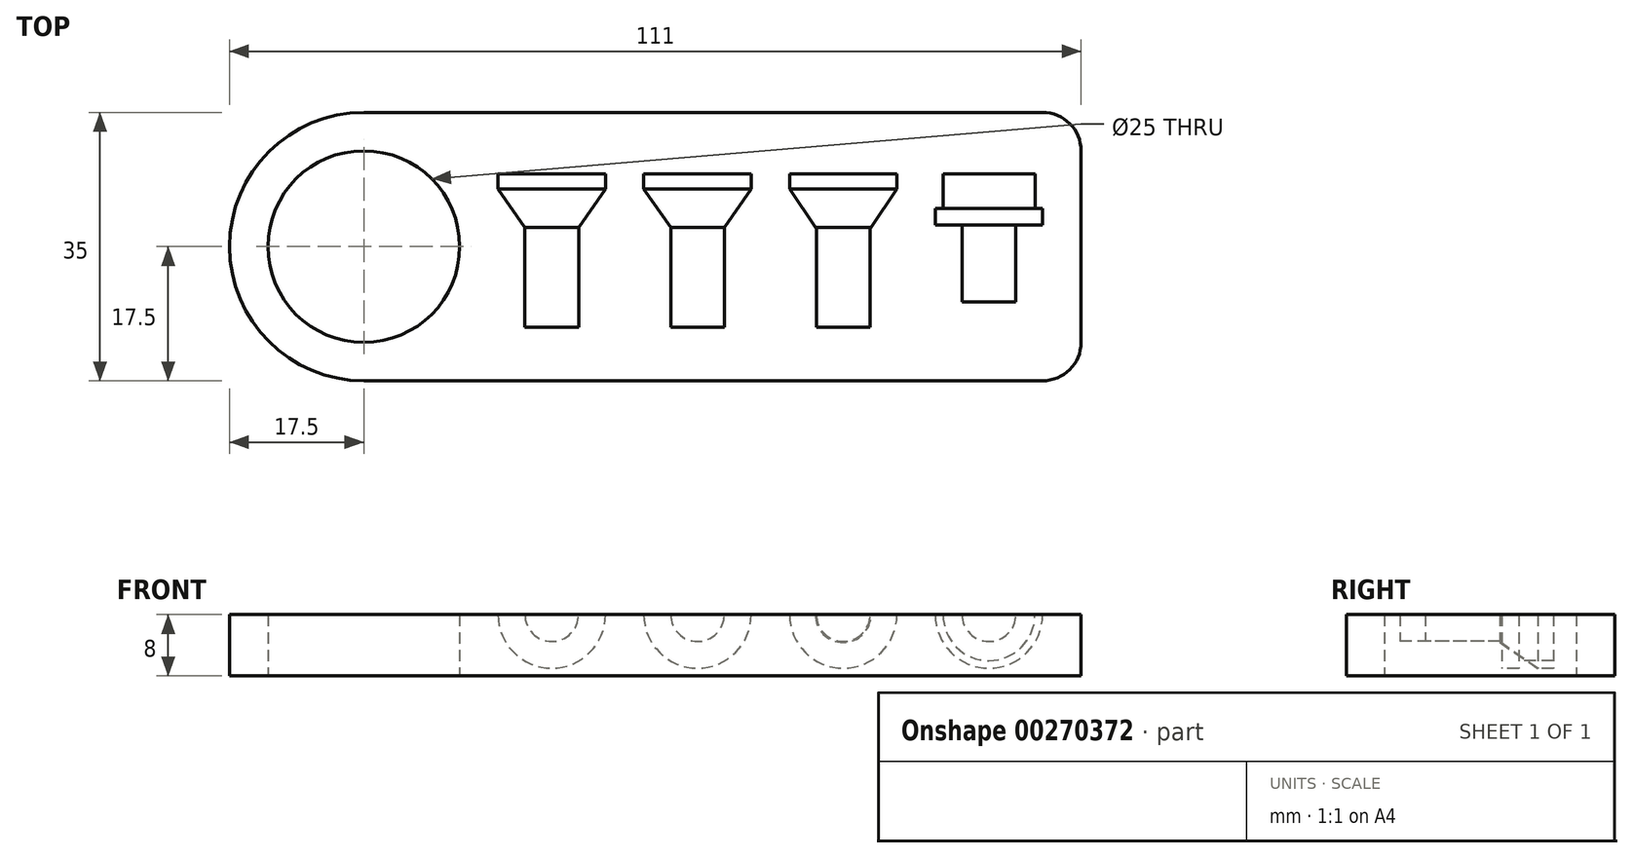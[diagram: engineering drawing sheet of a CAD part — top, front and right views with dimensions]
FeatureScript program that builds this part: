
annotation { "Feature Type Name" : "Feature", "Feature Type Description" : "" }
export const myFeature = defineFeature(function(context is Context, id is Id, definition is map)
    precondition{}
    {
        {
            var Q0;
            Q0=qCreatedBy(makeId("Top.planeOp"),FACE);
            var sketch = newSketch(context, id + "F0", { "sketchPlane" : qUnion([Q0])});
            skLineSegment(sketch, "E0.bottom", {"start": v(17.5, 0) * mm, "end": v(106, 0) * mm});
            skLineSegment(sketch, "E0.top", {"start": v(17.5, 35) * mm, "end": v(106, 35) * mm});
            skLineSegment(sketch, "E0.left", {"start": v(0, 17.5) * mm, "end": v(0, 17.5) * mm});
            skLineSegment(sketch, "E0.right", {"start": v(111, 5) * mm, "end": v(111, 30) * mm});
            skLineSegment(sketch, "E1.bottom", {"start": v(0, 0) * mm, "end": v(17.5, 0) * mm, "construction": true});
            skLineSegment(sketch, "E1.top", {"start": v(0, 17.5) * mm, "end": v(17.5, 17.5) * mm, "construction": true});
            skLineSegment(sketch, "E1.left", {"start": v(0, 0) * mm, "end": v(0, 17.5) * mm, "construction": true});
            skLineSegment(sketch, "E1.right", {"start": v(17.5, 0) * mm, "end": v(17.5, 17.5) * mm, "construction": true});
            skCircle(sketch, "E2", {"center": v(17.5, 17.5) * mm, "radius": 12.5 * mm});
            skPoint(sketch, "E3.visualSharp", {"position": v(0, 0) * mm});
            skArc(sketch, "E3.filletArc", {"start": v(0, 17.5) * mm, "mid": v(5.13, 5.13) * mm, "end": v(17.5, 0) * mm});
            skPoint(sketch, "E4.visualSharp", {"position": v(0, 35) * mm});
            skArc(sketch, "E4.filletArc", {"start": v(17.5, 35) * mm, "mid": v(5.13, 29.87) * mm, "end": v(0, 17.5) * mm});
            skPoint(sketch, "E5.visualSharp", {"position": v(111, 35) * mm});
            skArc(sketch, "E5.filletArc", {"start": v(111, 30) * mm, "mid": v(109.54, 33.54) * mm, "end": v(106, 35) * mm});
            skPoint(sketch, "E6.visualSharp", {"position": v(111, 0) * mm});
            skArc(sketch, "E6.filletArc", {"start": v(106, 0) * mm, "mid": v(109.54, 1.46) * mm, "end": v(111, 5) * mm});
            skSolve(sketch);
        }
        {
            var Q0;
            Q0=makeQuery(id+"F0.imprint","IMPRINT",FACE,{"disambiguationData":[TD([[makeQuery(id+"F0.imprint","IMPRINT",EDGE,{"derivedFrom":sQuery(id+"F0.wireOp",EDGE,"E0.bottom")}),1.0]])]});
            extrude(context, id + "F1", {"entities" : qUnion([Q0]), "depth" : 8 * mm});
        }
        {
            var Q0;
            Q0=makeQuery(id+"F1.opExtrude","CAP_FACE",FACE,{"disambiguationData":[OSD([sQuery(id+"F0.wireOp",EDGE,"E0.bottom"),sQuery(id+"F0.wireOp",EDGE,"E0.top"),sQuery(id+"F0.wireOp",EDGE,"E0.right"),sQuery(id+"F0.wireOp",EDGE,"E2"),sQuery(id+"F0.wireOp",EDGE,"E3.filletArc"),sQuery(id+"F0.wireOp",EDGE,"E4.filletArc"),sQuery(id+"F0.wireOp",EDGE,"E5.filletArc"),sQuery(id+"F0.wireOp",EDGE,"E6.filletArc")])],"isStart":false});
            var sketch = newSketch(context, id + "F2", { "sketchPlane" : qUnion([Q0])});
            skLineSegment(sketch, "E7.bottom", {"start": v(0, 0) * mm, "end": v(42, 0) * mm, "construction": true});
            skLineSegment(sketch, "E7.top", {"start": v(0, 27) * mm, "end": v(42, 27) * mm, "construction": true});
            skLineSegment(sketch, "E7.left", {"start": v(0, 0) * mm, "end": v(0, 27) * mm, "construction": true});
            skLineSegment(sketch, "E7.right", {"start": v(42, 0) * mm, "end": v(42, 27) * mm, "construction": true});
            skLineSegment(sketch, "E8.bottom", {"start": v(42, 27) * mm, "end": v(49, 27) * mm});
            skLineSegment(sketch, "E8.left", {"start": v(42, 27) * mm, "end": v(42, 25) * mm});
            skLineSegment(sketch, "E8.right", {"start": v(49, 27) * mm, "end": v(49, 25) * mm});
            skLineSegment(sketch, "E9", {"start": v(42, 27) * mm, "end": v(61, 27) * mm, "construction": true});
            skLineSegment(sketch, "E10", {"start": v(61, 27) * mm, "end": v(80, 27) * mm, "construction": true});
            skLineSegment(sketch, "E11.bottom", {"start": v(61, 27) * mm, "end": v(68, 27) * mm});
            skLineSegment(sketch, "E11.left", {"start": v(61, 27) * mm, "end": v(61, 25) * mm});
            skLineSegment(sketch, "E11.right", {"start": v(68, 27) * mm, "end": v(68, 25) * mm});
            skLineSegment(sketch, "E12.bottom", {"start": v(80, 27) * mm, "end": v(87, 27) * mm});
            skLineSegment(sketch, "E12.left", {"start": v(80, 27) * mm, "end": v(80, 25) * mm});
            skLineSegment(sketch, "E12.right", {"start": v(87, 27) * mm, "end": v(87, 25) * mm});
            skLineSegment(sketch, "E13.left", {"start": v(42, 25) * mm, "end": v(42, 20) * mm});
            skLineSegment(sketch, "E14.left", {"start": v(61, 25) * mm, "end": v(61, 20) * mm});
            skLineSegment(sketch, "E15.top", {"start": v(83.5, 20) * mm, "end": v(83.63, 20) * mm});
            skLineSegment(sketch, "E15.left", {"start": v(80, 25) * mm, "end": v(80, 20) * mm});
            skLineSegment(sketch, "E16.top", {"start": v(80, 7) * mm, "end": v(83.5, 7) * mm});
            skLineSegment(sketch, "E16.left", {"start": v(80, 20) * mm, "end": v(80, 7) * mm});
            skLineSegment(sketch, "E16.right", {"start": v(83.5, 20) * mm, "end": v(83.5, 7) * mm});
            skLineSegment(sketch, "E17.top", {"start": v(61, 7) * mm, "end": v(64.5, 7) * mm});
            skLineSegment(sketch, "E17.left", {"start": v(61, 20) * mm, "end": v(61, 7) * mm});
            skLineSegment(sketch, "E17.right", {"start": v(64.5, 20) * mm, "end": v(64.5, 7) * mm});
            skLineSegment(sketch, "E18.top", {"start": v(42, 7) * mm, "end": v(45.5, 7) * mm});
            skLineSegment(sketch, "E18.left", {"start": v(42, 20) * mm, "end": v(42, 7) * mm});
            skLineSegment(sketch, "E18.right", {"start": v(45.5, 20) * mm, "end": v(45.5, 7) * mm});
            skLineSegment(sketch, "E19", {"start": v(49, 25) * mm, "end": v(45.5, 20) * mm});
            skLineSegment(sketch, "E20", {"start": v(68, 25) * mm, "end": v(64.5, 20) * mm});
            skLineSegment(sketch, "E21", {"start": v(87, 25) * mm, "end": v(83.63, 20) * mm});
            skLineSegment(sketch, "E22", {"start": v(80, 27) * mm, "end": v(99, 27) * mm, "construction": true});
            skLineSegment(sketch, "E23.bottom", {"start": v(99, 27) * mm, "end": v(105, 27) * mm});
            skLineSegment(sketch, "E23.left", {"start": v(99, 27) * mm, "end": v(99, 22.5) * mm});
            skLineSegment(sketch, "E23.right", {"start": v(105, 27) * mm, "end": v(105, 22.5) * mm});
            skLineSegment(sketch, "E24.bottom", {"start": v(105, 22.5) * mm, "end": v(106, 22.5) * mm});
            skLineSegment(sketch, "E24.top", {"start": v(102.5, 20.3) * mm, "end": v(106, 20.3) * mm});
            skLineSegment(sketch, "E24.left", {"start": v(99, 22.5) * mm, "end": v(99, 20.3) * mm});
            skLineSegment(sketch, "E24.right", {"start": v(106, 22.5) * mm, "end": v(106, 20.3) * mm});
            skLineSegment(sketch, "E25.top", {"start": v(99, 10.3) * mm, "end": v(102.5, 10.3) * mm});
            skLineSegment(sketch, "E25.left", {"start": v(99, 20.3) * mm, "end": v(99, 10.3) * mm});
            skLineSegment(sketch, "E25.right", {"start": v(102.5, 20.3) * mm, "end": v(102.5, 10.3) * mm});
            skSolve(sketch);
        }
        {
            var Q0;
            Q0=makeQuery(id+"F2.imprint","IMPRINT",FACE,{"disambiguationData":[TD([[makeQuery(id+"F2.imprint","IMPRINT",EDGE,{"derivedFrom":sQuery(id+"F2.wireOp",EDGE,"E23.bottom")}),-1.0]])]});
            var Q1;
            Q1=sQuery(id+"F2.wireOp",EDGE,"E25.left");
            revolve(context, id + "F3", {"operationType" : NewBodyOperationType.REMOVE, "entities" : qUnion([Q0]), "axis" : qUnion([Q1]), "revolveType" : RevolveType.FULL, "oppositeDirection" : true});
        }
        {
            var Q0;
            Q0=makeQuery(id+"F2.imprint","IMPRINT",FACE,{"disambiguationData":[TD([[makeQuery(id+"F2.imprint","IMPRINT",EDGE,{"derivedFrom":sQuery(id+"F2.wireOp",EDGE,"E12.bottom")}),-1.0]])]});
            var Q1;
            Q1=sQuery(id+"F2.wireOp",EDGE,"E16.left");
            revolve(context, id + "F4", {"operationType" : NewBodyOperationType.REMOVE, "entities" : qUnion([Q0]), "axis" : qUnion([Q1]), "revolveType" : RevolveType.FULL, "oppositeDirection" : true});
        }
        {
            var Q0;
            Q0=makeQuery(id+"F2.imprint","IMPRINT",FACE,{"disambiguationData":[TD([[makeQuery(id+"F2.imprint","IMPRINT",EDGE,{"derivedFrom":sQuery(id+"F2.wireOp",EDGE,"E11.bottom")}),-1.0]])]});
            var Q1;
            Q1=sQuery(id+"F2.wireOp",EDGE,"E17.left");
            revolve(context, id + "F5", {"operationType" : NewBodyOperationType.REMOVE, "entities" : qUnion([Q0]), "axis" : qUnion([Q1]), "revolveType" : RevolveType.FULL, "oppositeDirection" : true});
        }
        {
            var Q0;
            Q0=makeQuery(id+"F2.imprint","IMPRINT",FACE,{"disambiguationData":[TD([[makeQuery(id+"F2.imprint","IMPRINT",EDGE,{"derivedFrom":sQuery(id+"F2.wireOp",EDGE,"E8.bottom")}),-1.0]])]});
            var Q1;
            Q1=sQuery(id+"F2.wireOp",EDGE,"E18.left");
            revolve(context, id + "F6", {"operationType" : NewBodyOperationType.REMOVE, "entities" : qUnion([Q0]), "axis" : qUnion([Q1]), "revolveType" : RevolveType.FULL, "oppositeDirection" : true});
        }
    });
